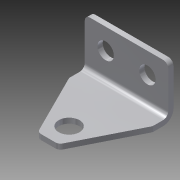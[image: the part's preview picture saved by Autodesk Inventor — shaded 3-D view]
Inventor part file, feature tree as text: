
AUTODESK INVENTOR PART (.ipt)
format: ipt  version: 2014 (Build 180170000, 170)  size: 156,160 bytes
history: native  units: in
note: dims shown in document units (in); Inventor stores cm internally (conversion verified against a paired STEP export)
features: sheet_metal_op x4, sketch x3, other x2, extrude x1, fillet x1
ambient origin geometry x8: Origin, YZ Plane, XZ Plane, XY Plane, X Axis, Y Axis, Z Axis, Center Point
bodies: Solid1 (feature_tree)
feature tree (11):
  sheet_metal_op  "Face1"
  sheet_metal_op  "Flange1"
  extrude  "Extrusion1"  Depth=0.5in
  fillet  "Fillet1"  Radius=0.196in
  sketch  "Sketch1"  dims[d0=1.0in d1=0.5in d2=0.196in]
  other  "Plate1"
  sketch  "Sketch2"  dims[d3=0.196in]
  other  "Plate2"
  sheet_metal_op  "Bend1"
  sheet_metal_op  "Corner1"
  sketch  "Sketch3"  dims[d4=0.25in d5=0.25in d6=0.25in d7=0.25in d8=0.0625in d9=0.0625in d10=0.0312in d11=0.125in d12=0.0625in d13=1.0in d14=90.0deg d15=0.0625in d16=0.25in d17=0.0625in d18=0.0625in d19=0.125in d20=0.125in d21=0.25in d22=0.25in d23=1.0in d24=0.0in d25=0.0625in]
